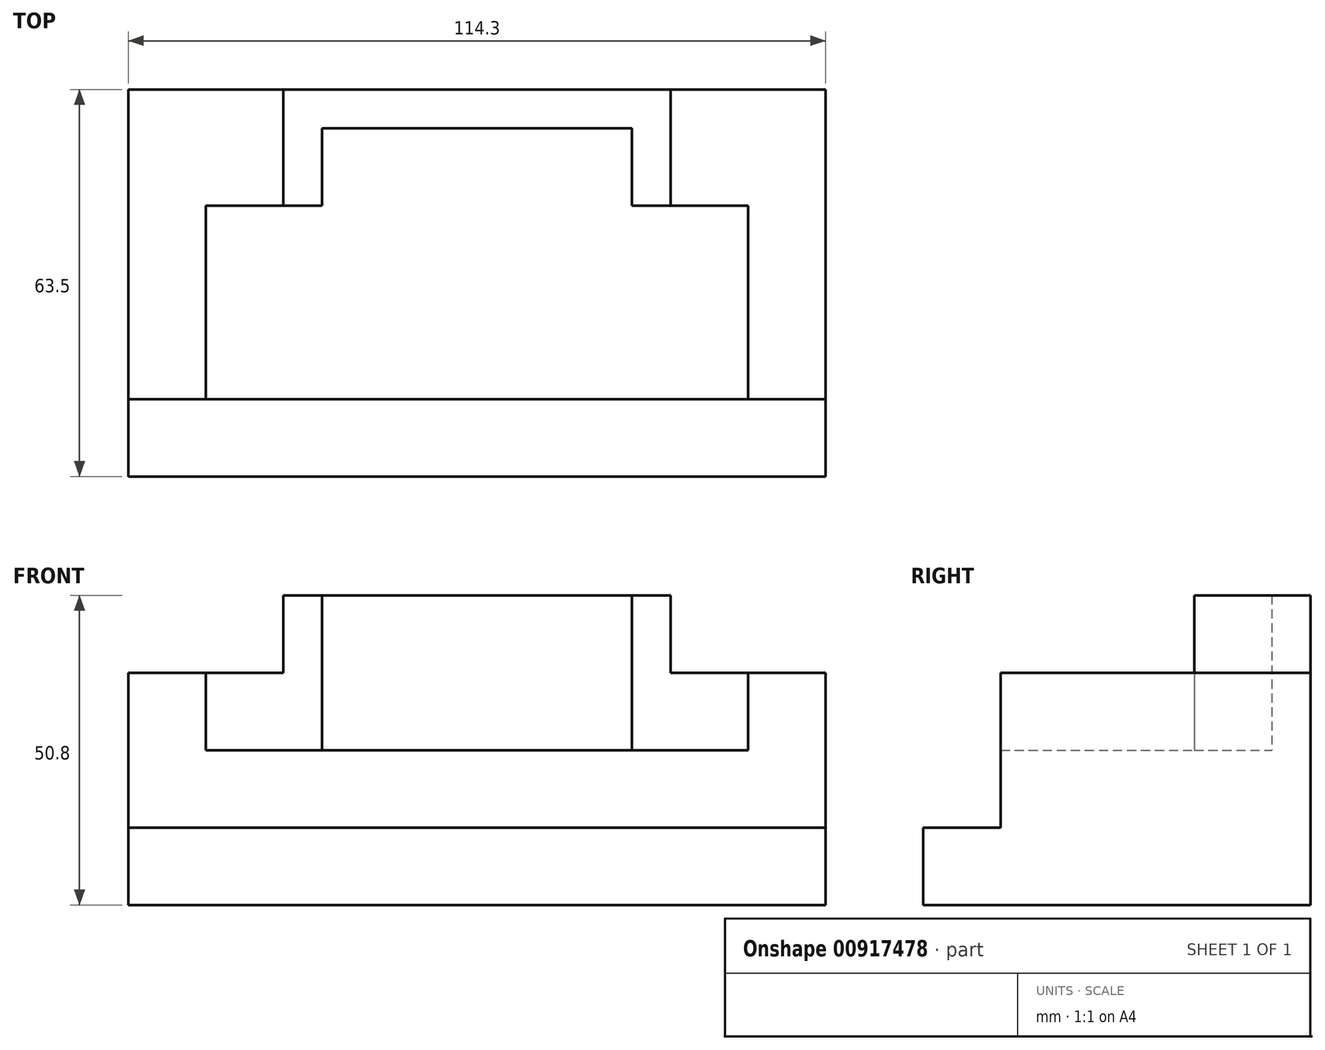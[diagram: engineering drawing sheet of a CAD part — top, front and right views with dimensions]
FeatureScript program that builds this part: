
annotation { "Feature Type Name" : "Feature", "Feature Type Description" : "" }
export const myFeature = defineFeature(function(context is Context, id is Id, definition is map)
    precondition{}
    {
        {
            var Q0;
            Q0=qCreatedBy(makeId("Top.planeOp"),FACE);
            var sketch = newSketch(context, id + "F0", { "sketchPlane" : qUnion([Q0])});
            skLineSegment(sketch, "E0.bottom", {"start": v(0, 0) * mm, "end": v(114.3, 0) * mm});
            skLineSegment(sketch, "E0.top", {"start": v(0, 63.5) * mm, "end": v(114.3, 63.5) * mm});
            skLineSegment(sketch, "E0.left", {"start": v(0, 0) * mm, "end": v(0, 63.5) * mm});
            skLineSegment(sketch, "E0.right", {"start": v(114.3, 0) * mm, "end": v(114.3, 63.5) * mm});
            skSolve(sketch);
        }
        {
            var Q0;
            Q0=makeQuery(id+"F0.imprint","IMPRINT",FACE,{"disambiguationData":[TD([[makeQuery(id+"F0.imprint","IMPRINT",EDGE,{"derivedFrom":sQuery(id+"F0.wireOp",EDGE,"E0.bottom")}),1.0]])]});
            extrude(context, id + "F1", {"entities" : qUnion([Q0]), "depth" : 12.7 * mm, "offsetDistance" : 25.4 * mm});
        }
        {
            var Q0;
            Q0=makeQuery(id+"F1.opExtrude","CAP_FACE",FACE,{"disambiguationData":[OSD([sQuery(id+"F0.wireOp",EDGE,"E0.bottom"),sQuery(id+"F0.wireOp",EDGE,"E0.top"),sQuery(id+"F0.wireOp",EDGE,"E0.left"),sQuery(id+"F0.wireOp",EDGE,"E0.right")])],"isStart":false});
            var sketch = newSketch(context, id + "F2", { "sketchPlane" : qUnion([Q0])});
            skLineSegment(sketch, "E1", {"start": v(0, 12.7) * mm, "end": v(114.3, 12.7) * mm});
            skSolve(sketch);
        }
        {
            var Q0;
            {var subQ0=sQuery(id+"F2.wireOp",EDGE,"E1");Q0=makeQuery(id+"F2.imprint","IMPRINT",FACE,{"disambiguationData":[TD([[makeQuery(id+"F2.imprint","IMPRINT",EDGE,{"derivedFrom":subQ0}),1.0]])]});}
            extrude(context, id + "F3", {"entities" : qUnion([Q0]), "operationType" : NewBodyOperationType.ADD, "depth" : 12.7 * mm, "offsetDistance" : 25.4 * mm});
        }
        {
            var Q0;
            Q0=makeQuery(id+"F3.opExtrude","CAP_FACE",FACE,{"disambiguationData":[OSD([sQuery(id+"F0.wireOp",EDGE,"E0.top"),sQuery(id+"F0.wireOp",EDGE,"E0.left"),sQuery(id+"F0.wireOp",EDGE,"E0.right"),sQuery(id+"F2.wireOp",EDGE,"E1")])],"isStart":false});
            var sketch = newSketch(context, id + "F4", { "sketchPlane" : qUnion([Q0])});
            skLineSegment(sketch, "E2", {"start": v(12.7, 12.7) * mm, "end": v(12.7, 44.45) * mm});
            skLineSegment(sketch, "E3", {"start": v(12.7, 44.45) * mm, "end": v(31.75, 44.45) * mm});
            skLineSegment(sketch, "E4", {"start": v(31.75, 44.45) * mm, "end": v(31.75, 57.15) * mm});
            skLineSegment(sketch, "E5", {"start": v(101.6, 12.7) * mm, "end": v(101.6, 44.45) * mm});
            skLineSegment(sketch, "E6", {"start": v(101.6, 44.45) * mm, "end": v(82.55, 44.45) * mm});
            skLineSegment(sketch, "E7", {"start": v(82.55, 44.45) * mm, "end": v(82.55, 57.15) * mm});
            skLineSegment(sketch, "E8", {"start": v(31.75, 57.15) * mm, "end": v(82.55, 57.15) * mm});
            skSolve(sketch);
        }
        {
            var Q0;
            {var subQ2=sQuery(id+"F4.wireOp",EDGE,"E2");Q0=makeQuery(id+"F4.imprint","IMPRINT",FACE,{"disambiguationData":[TD([[makeQuery(id+"F4.imprint","IMPRINT",EDGE,{"derivedFrom":subQ2}),1.0]])]});}
            extrude(context, id + "F5", {"entities" : qUnion([Q0]), "operationType" : NewBodyOperationType.ADD, "depth" : 12.7 * mm, "offsetDistance" : 25.4 * mm});
        }
        {
            var Q0;
            Q0=makeQuery(id+"F5.opExtrude","CAP_FACE",FACE,{"disambiguationData":[OSD([sQuery(id+"F0.wireOp",EDGE,"E0.top"),sQuery(id+"F0.wireOp",EDGE,"E0.left"),sQuery(id+"F0.wireOp",EDGE,"E0.right"),sQuery(id+"F2.wireOp",EDGE,"E1"),sQuery(id+"F4.wireOp",EDGE,"E2"),sQuery(id+"F4.wireOp",EDGE,"E3"),sQuery(id+"F4.wireOp",EDGE,"E4"),sQuery(id+"F4.wireOp",EDGE,"E5"),sQuery(id+"F4.wireOp",EDGE,"E6"),sQuery(id+"F4.wireOp",EDGE,"E7"),sQuery(id+"F4.wireOp",EDGE,"E8")])],"isStart":false});
            var sketch = newSketch(context, id + "F6", { "sketchPlane" : qUnion([Q0])});
            skLineSegment(sketch, "E9", {"start": v(25.4, 44.45) * mm, "end": v(25.4, 63.5) * mm});
            skLineSegment(sketch, "E10", {"start": v(88.9, 44.45) * mm, "end": v(88.9, 63.5) * mm});
            skSolve(sketch);
        }
        {
            var Q0;
            {var subQ5=sQuery(id+"F6.wireOp",EDGE,"E9");Q0=makeQuery(id+"F6.imprint","IMPRINT",FACE,{"disambiguationData":[TD([[makeQuery(id+"F6.imprint","IMPRINT",EDGE,{"derivedFrom":subQ5}),-1.0]])]});}
            extrude(context, id + "F7", {"entities" : qUnion([Q0]), "operationType" : NewBodyOperationType.ADD, "depth" : 12.7 * mm, "offsetDistance" : 25.4 * mm});
        }
    });
